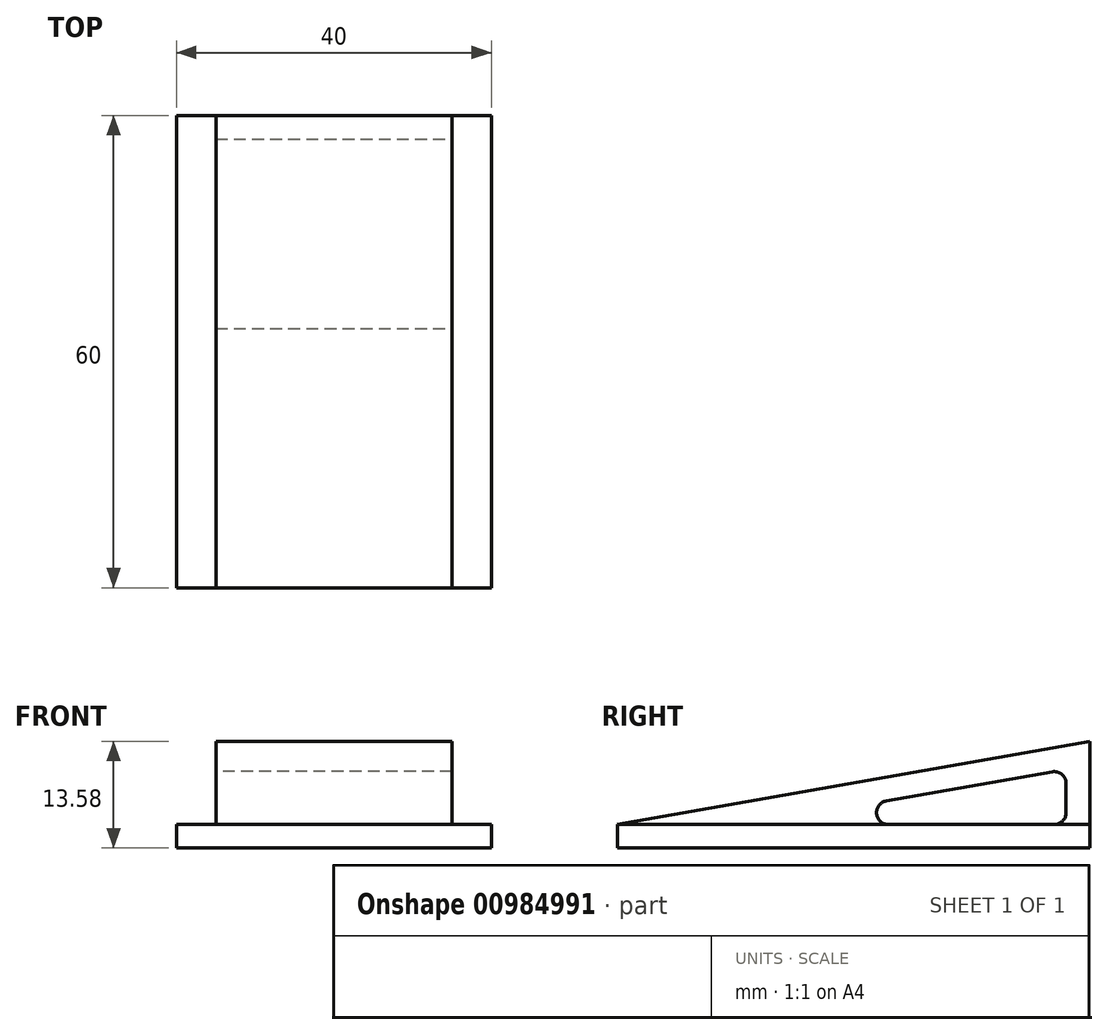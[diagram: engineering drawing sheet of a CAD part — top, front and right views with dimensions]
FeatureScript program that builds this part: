
annotation { "Feature Type Name" : "Feature", "Feature Type Description" : "" }
export const myFeature = defineFeature(function(context is Context, id is Id, definition is map)
    precondition{}
    {
        {
            assignVariable(context, id + "F0", {"name" : "t", "anyValue" : 3});
        }
        {
            assignVariable(context, id + "F1", {"name" : "offset", "anyValue" : 5});
        }
        {
            var Q0;
            Q0=qCreatedBy(makeId("Top.planeOp"),FACE);
            var sketch = newSketch(context, id + "F2", { "sketchPlane" : qUnion([Q0])});
            skLineSegment(sketch, "E0.bottom", {"start": v(-20, 0) * mm, "end": v(20, 0) * mm});
            skLineSegment(sketch, "E0.top", {"start": v(-20, 60) * mm, "end": v(20, 60) * mm});
            skLineSegment(sketch, "E0.left", {"start": v(-20, 0) * mm, "end": v(-20, 60) * mm});
            skLineSegment(sketch, "E0.right", {"start": v(20, 0) * mm, "end": v(20, 60) * mm});
            skSolve(sketch);
        }
        {
            var Q0;
            Q0=makeQuery(id+"F2.imprint","IMPRINT",FACE,{"disambiguationData":[TD([[makeQuery(id+"F2.imprint","IMPRINT",EDGE,{"derivedFrom":sQuery(id+"F2.wireOp",EDGE,"E0.bottom")}),1.0]])]});
            extrude(context, id + "F3", {"entities" : qUnion([Q0]), "depth" : (getVariable(context, 't')) * mm, "offsetDistance" : 25 * mm});
        }
        {
            var Q0;
            Q0=qCreatedBy(makeId("Right.planeOp"),FACE);
            var sketch = newSketch(context, id + "F4", { "sketchPlane" : qUnion([Q0])});
            skLineSegment(sketch, "E1", {"start": v(60, 13.58) * mm, "end": v(0, 3) * mm});
            skLineSegment(sketch, "E2", {"start": v(0, 3) * mm, "end": v(60, 3) * mm});
            skLineSegment(sketch, "E3", {"start": v(60, 3) * mm, "end": v(60, 13.58) * mm});
            skSolve(sketch);
        }
        {
            var Q0;
            Q0=makeQuery(id+"F4.imprint","IMPRINT",FACE,{"disambiguationData":[TD([[makeQuery(id+"F4.imprint","IMPRINT",EDGE,{"derivedFrom":sQuery(id+"F4.wireOp",EDGE,"E1")}),1.0]])]});
            var Q1;
            Q1=sQuery(id+"F4.wireOp",EDGE,"E1");
            var Q2;
            Q2=makeQuery(id+"F3.opExtrude","SWEPT_FACE",FACE,{"disambiguationData":[OSD([sQuery(id+"F2.wireOp",EDGE,"E0.right")])]});
            var Q3;
            Q3=makeQuery(id+"F3.opExtrude","SWEPT_FACE",FACE,{"disambiguationData":[OSD([sQuery(id+"F2.wireOp",EDGE,"E0.left")])]});
            extrude(context, id + "F5", {"entities" : qUnion([Q0]), "operationType" : NewBodyOperationType.ADD, "surfaceEntities" : qUnion([Q1]), "endBound" : BoundingType.UP_TO_SURFACE, "depth" : 25 * mm, "endBoundEntityFace" : qUnion([Q2]), "hasOffset" : true, "offsetDistance" : (getVariable(context, 'offset')) * mm, "hasSecondDirection" : true, "secondDirectionBound" : SecondDirectionBoundingType.UP_TO_SURFACE, "secondDirectionOppositeDirection" : true, "secondDirectionDepth" : 25 * mm, "secondDirectionBoundEntityFace" : qUnion([Q3]), "hasSecondDirectionOffset" : true, "secondDirectionOffsetDistance" : (getVariable(context, 'offset')) * mm});
        }
        {
            var Q0;
            Q0=makeQuery(id+"F5.opExtrude","CAP_FACE",FACE,{"disambiguationData":[OSD([sQuery(id+"F4.wireOp",EDGE,"E1"),sQuery(id+"F4.wireOp",EDGE,"E2"),sQuery(id+"F4.wireOp",EDGE,"E3")])],"isStart":false});
            var sketch = newSketch(context, id + "F6", { "sketchPlane" : qUnion([Q0])});
            skLineSegment(sketch, "E4", {"start": v(57, 3) * mm, "end": v(57, 10) * mm});
            skLineSegment(sketch, "E5", {"start": v(57, 10) * mm, "end": v(17.28, 3) * mm});
            skLineSegment(sketch, "E6", {"start": v(17.28, 3) * mm, "end": v(57, 3) * mm});
            skSolve(sketch);
        }
        {
            var Q0;
            Q0=makeQuery(id+"F6.imprint","IMPRINT",FACE,{"disambiguationData":[TD([[makeQuery(id+"F6.imprint","IMPRINT",EDGE,{"derivedFrom":sQuery(id+"F6.wireOp",EDGE,"E4")}),1.0]])]});
            extrude(context, id + "F7", {"entities" : qUnion([Q0]), "operationType" : NewBodyOperationType.REMOVE, "endBound" : BoundingType.UP_TO_NEXT, "oppositeDirection" : true, "depth" : 25 * mm, "offsetDistance" : 25 * mm});
        }
        {
            var Q0;
            Q0=makeQuery(id+"F7.boolean.opBoolean","COPY",EDGE,{"derivedFrom":makeQuery(id+"F7.opExtrude","SWEPT_EDGE",EDGE,{"disambiguationData":[OSD([sQuery(id+"F4.wireOp",EDGE,"E2"),sQuery(id+"F6.wireOp",EDGE,"E4"),sQuery(id+"F6.wireOp",EDGE,"E6")])]})});
            var Q1;
            Q1=makeQuery(id+"F7.boolean.opBoolean","COPY",EDGE,{"derivedFrom":makeQuery(id+"F7.opExtrude","SWEPT_EDGE",EDGE,{"disambiguationData":[OSD([sQuery(id+"F6.wireOp",EDGE,"E4"),sQuery(id+"F6.wireOp",EDGE,"E5")])]})});
            var Q2;
            Q2=makeQuery(id+"F7.boolean.opBoolean","COPY",EDGE,{"derivedFrom":makeQuery(id+"F7.opExtrude","SWEPT_EDGE",EDGE,{"disambiguationData":[OSD([sQuery(id+"F4.wireOp",EDGE,"E2"),sQuery(id+"F6.wireOp",EDGE,"E5"),sQuery(id+"F6.wireOp",EDGE,"E6")])]})});
            fillet(context, id + "F8", {"entities" : qUnion([Q0, Q1, Q2]), "radius" : 1.5 * mm, "tangentPropagation" : true, "allowEdgeOverflow" : false});
        }
    });
